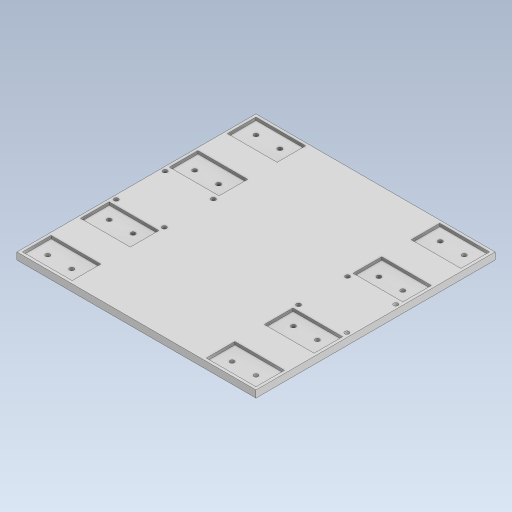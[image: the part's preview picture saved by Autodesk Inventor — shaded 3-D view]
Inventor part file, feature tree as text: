
AUTODESK INVENTOR PART (.ipt)
format: ipt  version: 2023.5 (Build 275446000, 446)  size: 214,016 bytes
history: native  units: in
note: dims shown in document units (in); Inventor stores cm internally (conversion verified against a paired STEP export)
features: extrude x4, sketch x1
ambient origin geometry x8: Origin, YZ Plane, XZ Plane, XY Plane, X Axis, Y Axis, Z Axis, Center Point
bodies: Body1 (feature_tree)
feature tree (5):
  sketch  "Sketch2"  dims[d17=6.6929in d18=6.6929in d19=1.3898in d20=0.7992in d21=0.0787in d22=0.0787in d23=0.7992in d24=0.8268in d25=0.1181in d26=0.3543in d27=0.3543in d28=0.1181in d29=0.6693in d30=0.1181in d31=0.3543in d32=0.3543in d33=0.1181in d34=0.1969in d35=0.0in d36=0.1181in d37=0.0in d38=0.1181in d39=0.1181in d40=0.1575in d41=1.3701in d42=0.1969in d43=0.0in d44=0.1181in d45=0.1181in d46=1.3504in d47=0.1969in d48=0.0in d13=0.0197in d14=0.0344in d15=0.0197in d16=0.0344in]
  extrude  "Extrusion3"  Depth=6.6929in
  extrude  "Extrusion4"  Depth=1.3898in
  extrude  "Extrusion5"  Depth=0.7992in
  extrude  "Extrusion6"  Depth=0.0787in
